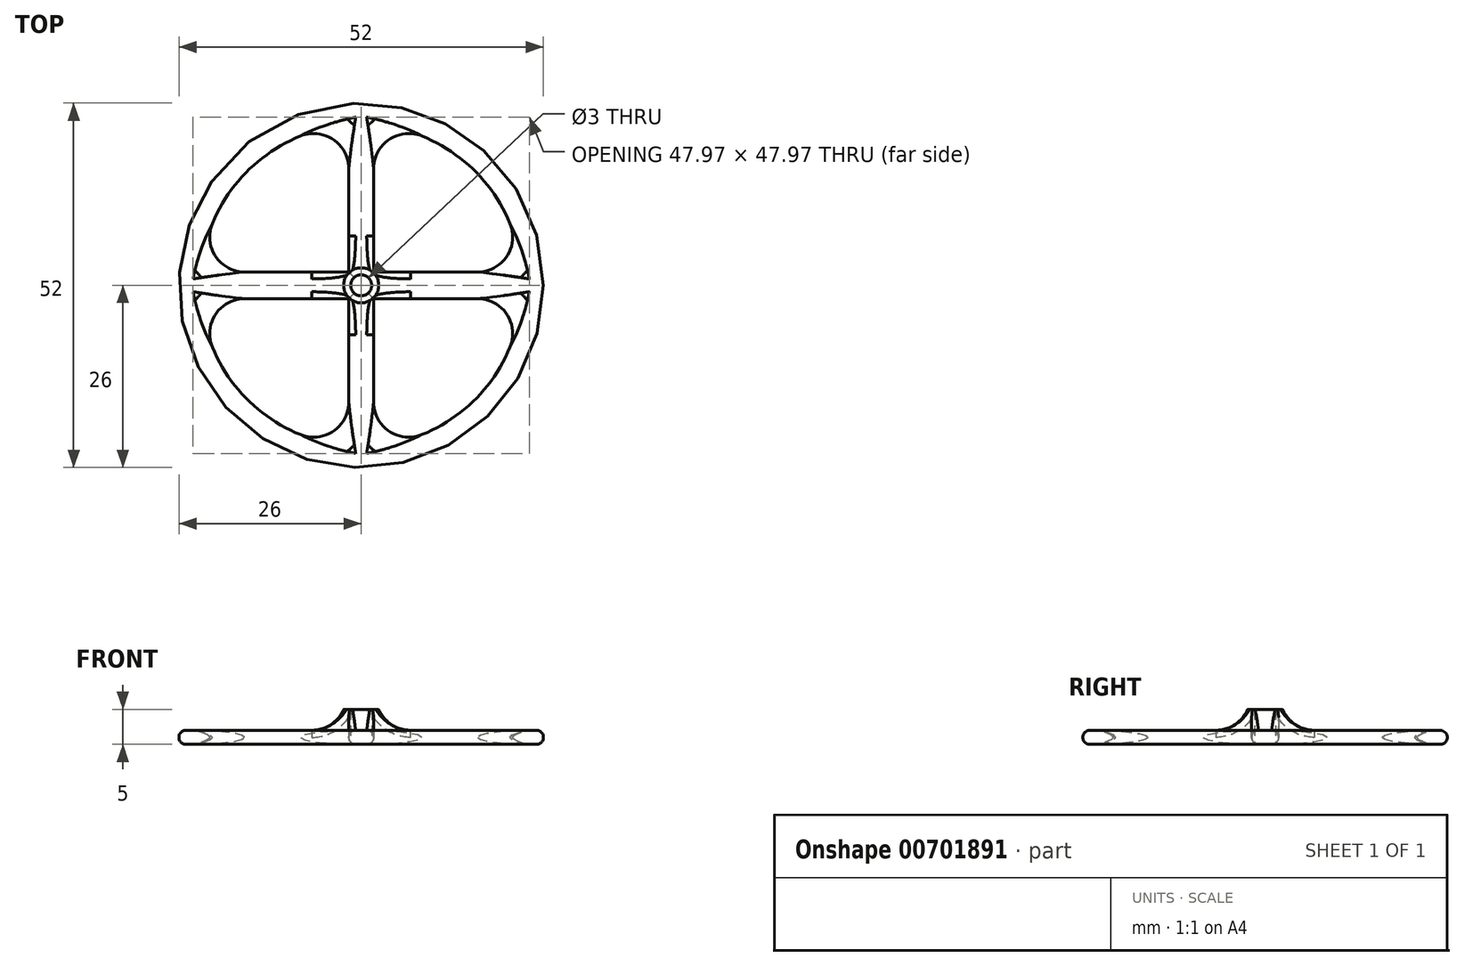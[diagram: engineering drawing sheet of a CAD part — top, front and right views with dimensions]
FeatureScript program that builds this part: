
annotation { "Feature Type Name" : "Feature", "Feature Type Description" : "" }
export const myFeature = defineFeature(function(context is Context, id is Id, definition is map)
    precondition{}
    {
        {
            var Q0;
            Q0=qCreatedBy(makeId("Top.planeOp"),FACE);
            var sketch = newSketch(context, id + "F0", { "sketchPlane" : qUnion([Q0])});
            skCircle(sketch, "E0", {"center": v(0, 0) * mm, "radius": 26 * mm});
            skLineSegment(sketch, "E1.bottom", {"start": v(1.78, -25.94) * mm, "end": v(-1.78, -25.94) * mm});
            skLineSegment(sketch, "E1.top", {"start": v(1.78, 25.94) * mm, "end": v(-1.78, 25.94) * mm});
            skLineSegment(sketch, "E1.left", {"start": v(1.78, -25.94) * mm, "end": v(1.78, 25.94) * mm});
            skLineSegment(sketch, "E1.right", {"start": v(-1.78, -25.94) * mm, "end": v(-1.78, 25.94) * mm});
            skLineSegment(sketch, "E2.bottom", {"start": v(25.93, -1.91) * mm, "end": v(-25.93, -1.91) * mm});
            skLineSegment(sketch, "E2.top", {"start": v(25.93, 1.91) * mm, "end": v(-25.93, 1.91) * mm});
            skLineSegment(sketch, "E2.left", {"start": v(25.93, -1.91) * mm, "end": v(25.93, 1.91) * mm});
            skLineSegment(sketch, "E2.right", {"start": v(-25.93, -1.91) * mm, "end": v(-25.93, 1.91) * mm});
            skCircle(sketch, "E3", {"center": v(0, 0) * mm, "radius": 1.57 * mm});
            skCircle(sketch, "E4", {"center": v(0, 0) * mm, "radius": 23 * mm});
            skSolve(sketch);
        }
        {
            var Q0;
            {var subQ0=sQuery(id+"F0.wireOp",EDGE,"E2.right");Q0=makeQuery(id+"F0.imprint","IMPRINT",FACE,{"disambiguationData":[TD([[makeQuery(id+"F0.imprint","IMPRINT",EDGE,{"derivedFrom":subQ0}),1.0]])]});}
            var Q1;
            {var subQ0=sQuery(id+"F0.wireOp",EDGE,"E2.right");Q1=makeQuery(id+"F0.imprint","IMPRINT",FACE,{"disambiguationData":[TD([[makeQuery(id+"F0.imprint","IMPRINT",EDGE,{"derivedFrom":subQ0}),-1.0]])]});}
            var Q2;
            {var subQ0=sQuery(id+"F0.wireOp",EDGE,"E1.right");var subQ5=sQuery(id+"F0.wireOp",EDGE,"E4");var subQ6=makeQuery(id+"F0.imprint","INTERSECT",VERTEX,{"disambiguationData":[OD(1.0)],"derivedFrom":[subQ0,subQ5]});Q2=makeQuery(id+"F0.imprint","IMPRINT",FACE,{"disambiguationData":[TD([[makeQuery(id+"F0.imprint","IMPRINT",EDGE,{"disambiguationData":[TD([[subQ6,-1.0]])],"derivedFrom":subQ5}),-1.0]])]});}
            var Q3;
            {var subQ0=sQuery(id+"F0.wireOp",EDGE,"E1.top");Q3=makeQuery(id+"F0.imprint","IMPRINT",FACE,{"disambiguationData":[TD([[makeQuery(id+"F0.imprint","IMPRINT",EDGE,{"derivedFrom":subQ0}),1.0]])]});}
            var Q4;
            {var subQ0=sQuery(id+"F0.wireOp",EDGE,"E1.top");Q4=makeQuery(id+"F0.imprint","IMPRINT",FACE,{"disambiguationData":[TD([[makeQuery(id+"F0.imprint","IMPRINT",EDGE,{"derivedFrom":subQ0}),-1.0]])]});}
            var Q5;
            {var subQ0=sQuery(id+"F0.wireOp",EDGE,"E2.left");Q5=makeQuery(id+"F0.imprint","IMPRINT",FACE,{"disambiguationData":[TD([[makeQuery(id+"F0.imprint","IMPRINT",EDGE,{"derivedFrom":subQ0}),-1.0]])]});}
            var Q6;
            {var subQ0=sQuery(id+"F0.wireOp",EDGE,"E2.left");Q6=makeQuery(id+"F0.imprint","IMPRINT",FACE,{"disambiguationData":[TD([[makeQuery(id+"F0.imprint","IMPRINT",EDGE,{"derivedFrom":subQ0}),1.0]])]});}
            var Q7;
            {var subQ0=sQuery(id+"F0.wireOp",EDGE,"E1.left");var subQ5=sQuery(id+"F0.wireOp",EDGE,"E4");var subQ7=makeQuery(id+"F0.imprint","INTERSECT",VERTEX,{"disambiguationData":[OD(1.0)],"derivedFrom":[subQ0,subQ5]});Q7=makeQuery(id+"F0.imprint","IMPRINT",FACE,{"disambiguationData":[TD([[makeQuery(id+"F0.imprint","IMPRINT",EDGE,{"disambiguationData":[TD([[subQ7,1.0]])],"derivedFrom":subQ5}),-1.0]])]});}
            var Q8;
            {var subQ0=sQuery(id+"F0.wireOp",EDGE,"E2.top");var subQ1=sQuery(id+"F0.wireOp",EDGE,"E1.left");var subQ2=makeQuery(id+"F0.imprint","INTERSECT",VERTEX,{"derivedFrom":[subQ1,subQ0]});Q8=makeQuery(id+"F0.imprint","IMPRINT",FACE,{"disambiguationData":[TD([[makeQuery(id+"F0.imprint","IMPRINT",EDGE,{"disambiguationData":[TD([[subQ2,-1.0]])],"derivedFrom":subQ1}),1.0]])]});}
            var Q9;
            Q9=makeQuery(id+"F0.imprint","IMPRINT",FACE,{"disambiguationData":[TD([[makeQuery(id+"F0.imprint","IMPRINT",EDGE,{"derivedFrom":sQuery(id+"F0.wireOp",EDGE,"E3")}),-1.0]])]});
            var Q10;
            {var subQ0=sQuery(id+"F0.wireOp",EDGE,"E2.bottom");var subQ1=sQuery(id+"F0.wireOp",EDGE,"E1.left");var subQ2=makeQuery(id+"F0.imprint","INTERSECT",VERTEX,{"derivedFrom":[subQ1,subQ0]});Q10=makeQuery(id+"F0.imprint","IMPRINT",FACE,{"disambiguationData":[TD([[makeQuery(id+"F0.imprint","IMPRINT",EDGE,{"disambiguationData":[TD([[subQ2,-1.0]])],"derivedFrom":subQ1}),-1.0]])]});}
            var Q11;
            {var subQ0=sQuery(id+"F0.wireOp",EDGE,"E2.bottom");var subQ1=sQuery(id+"F0.wireOp",EDGE,"E1.right");var subQ2=makeQuery(id+"F0.imprint","INTERSECT",VERTEX,{"derivedFrom":[subQ1,subQ0]});Q11=makeQuery(id+"F0.imprint","IMPRINT",FACE,{"disambiguationData":[TD([[makeQuery(id+"F0.imprint","IMPRINT",EDGE,{"disambiguationData":[TD([[subQ2,-1.0]])],"derivedFrom":subQ1}),1.0]])]});}
            var Q12;
            {var subQ0=sQuery(id+"F0.wireOp",EDGE,"E4");var subQ1=sQuery(id+"F0.wireOp",EDGE,"E1.left");var subQ2=makeQuery(id+"F0.imprint","INTERSECT",VERTEX,{"disambiguationData":[OD(0.0)],"derivedFrom":[subQ1,subQ0]});Q12=makeQuery(id+"F0.imprint","IMPRINT",FACE,{"disambiguationData":[TD([[makeQuery(id+"F0.imprint","IMPRINT",EDGE,{"disambiguationData":[TD([[subQ2,-1.0]])],"derivedFrom":subQ1}),1.0]])]});}
            var Q13;
            {var subQ0=sQuery(id+"F0.wireOp",EDGE,"E1.right");var subQ5=sQuery(id+"F0.wireOp",EDGE,"E4");var subQ7=makeQuery(id+"F0.imprint","INTERSECT",VERTEX,{"disambiguationData":[OD(0.0)],"derivedFrom":[subQ0,subQ5]});Q13=makeQuery(id+"F0.imprint","IMPRINT",FACE,{"disambiguationData":[TD([[makeQuery(id+"F0.imprint","IMPRINT",EDGE,{"disambiguationData":[TD([[subQ7,1.0]])],"derivedFrom":subQ5}),-1.0]])]});}
            var Q14;
            {var subQ0=sQuery(id+"F0.wireOp",EDGE,"E1.bottom");Q14=makeQuery(id+"F0.imprint","IMPRINT",FACE,{"disambiguationData":[TD([[makeQuery(id+"F0.imprint","IMPRINT",EDGE,{"derivedFrom":subQ0}),-1.0]])]});}
            var Q15;
            {var subQ0=sQuery(id+"F0.wireOp",EDGE,"E1.bottom");Q15=makeQuery(id+"F0.imprint","IMPRINT",FACE,{"disambiguationData":[TD([[makeQuery(id+"F0.imprint","IMPRINT",EDGE,{"derivedFrom":subQ0}),1.0]])]});}
            var Q16;
            {var subQ0=sQuery(id+"F0.wireOp",EDGE,"E1.left");var subQ5=sQuery(id+"F0.wireOp",EDGE,"E4");var subQ6=makeQuery(id+"F0.imprint","INTERSECT",VERTEX,{"disambiguationData":[OD(0.0)],"derivedFrom":[subQ0,subQ5]});Q16=makeQuery(id+"F0.imprint","IMPRINT",FACE,{"disambiguationData":[TD([[makeQuery(id+"F0.imprint","IMPRINT",EDGE,{"disambiguationData":[TD([[subQ6,-1.0]])],"derivedFrom":subQ5}),-1.0]])]});}
            extrude(context, id + "F1", {"entities" : qUnion([Q0, Q1, Q2, Q3, Q4, Q5, Q6, Q7, Q8, Q9, Q10, Q11, Q12, Q13, Q14, Q15, Q16]), "depth" : 2 * mm, "offsetDistance" : 25 * mm});
        }
        {
            var Q0;
            Q0=qCreatedBy(makeId("Top.planeOp"),FACE);
            var sketch = newSketch(context, id + "F2", { "sketchPlane" : qUnion([Q0])});
            skCircle(sketch, "E5", {"center": v(0, 0) * mm, "radius": 2.5 * mm});
            skSolve(sketch);
        }
        {
            var Q0;
            Q0=makeQuery(id+"F2.imprint","IMPRINT",FACE,{"disambiguationData":[TD([[makeQuery(id+"F2.imprint","IMPRINT",EDGE,{"derivedFrom":sQuery(id+"F2.wireOp",EDGE,"E5")}),1.0]])]});
            extrude(context, id + "F3", {"entities" : qUnion([Q0]), "operationType" : NewBodyOperationType.ADD, "depth" : 5 * mm, "offsetDistance" : 25 * mm});
        }
        {
            var Q0;
            Q0=qCreatedBy(makeId("Top.planeOp"),FACE);
            var sketch = newSketch(context, id + "F4", { "sketchPlane" : qUnion([Q0])});
            skCircle(sketch, "E6", {"center": v(0, 0) * mm, "radius": 1.5 * mm});
            skSolve(sketch);
        }
        {
            var Q0;
            Q0=makeQuery(id+"F4.imprint","IMPRINT",FACE,{"disambiguationData":[TD([[makeQuery(id+"F4.imprint","IMPRINT",EDGE,{"derivedFrom":sQuery(id+"F4.wireOp",EDGE,"E6")}),1.0]])]});
            extrude(context, id + "F5", {"entities" : qUnion([Q0]), "operationType" : NewBodyOperationType.REMOVE, "depth" : 5 * mm, "offsetDistance" : 25 * mm});
        }
        {
            var Q0;
            Q0=makeQuery(id+"F1.opExtrude","CAP_EDGE",EDGE,{"disambiguationData":[OSD([sQuery(id+"F0.wireOp",EDGE,"E0")])],"isStart":false});
            fillet(context, id + "F6", {"entities" : qUnion([Q0]), "tangentPropagation" : true, "radius" : 1 * mm, "defaultsChanged" : true, "vertexSettings" : [], "allowEdgeOverflow" : false});
        }
        {
            var Q0;
            Q0=makeQuery(id+"F1.opExtrude","CAP_EDGE",EDGE,{"disambiguationData":[OSD([sQuery(id+"F0.wireOp",EDGE,"E0")])],"isStart":true});
            fillet(context, id + "F7", {"entities" : qUnion([Q0]), "tangentPropagation" : true, "radius" : 1 * mm, "defaultsChanged" : true, "vertexSettings" : [], "allowEdgeOverflow" : false});
        }
        {
            var Q0;
            Q0=makeQuery(id+"F3.boolean.opBoolean","INTERSECT",EDGE,{"derivedFrom":[makeQuery(id+"F1.opExtrude","CAP_FACE",FACE,{"disambiguationData":[OSD([sQuery(id+"F0.wireOp",EDGE,"E0"),sQuery(id+"F0.wireOp",EDGE,"E1.left"),sQuery(id+"F0.wireOp",EDGE,"E1.right"),sQuery(id+"F0.wireOp",EDGE,"E2.bottom"),sQuery(id+"F0.wireOp",EDGE,"E2.top"),sQuery(id+"F0.wireOp",EDGE,"E3"),sQuery(id+"F0.wireOp",EDGE,"E4")])],"isStart":false}),makeQuery(id+"F3.opExtrude","SWEPT_FACE",FACE,{"disambiguationData":[OSD([sQuery(id+"F2.wireOp",EDGE,"E5")])]})]});
            fillet(context, id + "F8", {"entities" : qUnion([Q0]), "tangentPropagation" : true, "radius" : 5 * mm, "defaultsChanged" : false, "vertexSettings" : [], "allowEdgeOverflow" : false});
        }
        {
            var Q0;
            {var subQ0=sQuery(id+"F0.wireOp",EDGE,"E1.right");Q0=makeQuery(id+"F1.opExtrude","CAP_EDGE",EDGE,{"disambiguationData":[OSD([subQ0]),TDD([makeQuery(id+"F0.imprint","IMPRINT",EDGE,{"disambiguationData":[TD([[makeQuery(id+"F0.imprint","INTERSECT",VERTEX,{"disambiguationData":[OD(0.0)],"derivedFrom":[subQ0,sQuery(id+"F0.wireOp",EDGE,"E4")]}),-1.0]])],"derivedFrom":subQ0})])],"isStart":true});}
            var Q1;
            {var subQ0=sQuery(id+"F0.wireOp",EDGE,"E1.left");Q1=makeQuery(id+"F1.opExtrude","CAP_EDGE",EDGE,{"disambiguationData":[OSD([subQ0]),TDD([makeQuery(id+"F0.imprint","IMPRINT",EDGE,{"disambiguationData":[TD([[makeQuery(id+"F0.imprint","INTERSECT",VERTEX,{"disambiguationData":[OD(0.0)],"derivedFrom":[subQ0,sQuery(id+"F0.wireOp",EDGE,"E4")]}),-1.0]])],"derivedFrom":subQ0})])],"isStart":true});}
            var Q2;
            {var subQ0=sQuery(id+"F0.wireOp",EDGE,"E1.left");Q2=makeQuery(id+"F1.opExtrude","CAP_EDGE",EDGE,{"disambiguationData":[OSD([subQ0]),TDD([makeQuery(id+"F0.imprint","IMPRINT",EDGE,{"disambiguationData":[TD([[makeQuery(id+"F0.imprint","INTERSECT",VERTEX,{"derivedFrom":[subQ0,sQuery(id+"F0.wireOp",EDGE,"E2.top")]}),-1.0]])],"derivedFrom":subQ0})])],"isStart":true});}
            var Q3;
            {var subQ0=sQuery(id+"F0.wireOp",EDGE,"E1.right");Q3=makeQuery(id+"F1.opExtrude","CAP_EDGE",EDGE,{"disambiguationData":[OSD([subQ0]),TDD([makeQuery(id+"F0.imprint","IMPRINT",EDGE,{"disambiguationData":[TD([[makeQuery(id+"F0.imprint","INTERSECT",VERTEX,{"derivedFrom":[subQ0,sQuery(id+"F0.wireOp",EDGE,"E2.top")]}),-1.0]])],"derivedFrom":subQ0})])],"isStart":true});}
            var Q4;
            {var subQ0=sQuery(id+"F0.wireOp",EDGE,"E2.bottom");Q4=makeQuery(id+"F1.opExtrude","CAP_EDGE",EDGE,{"disambiguationData":[OSD([subQ0]),TDD([makeQuery(id+"F0.imprint","IMPRINT",EDGE,{"disambiguationData":[TD([[makeQuery(id+"F0.imprint","INTERSECT",VERTEX,{"derivedFrom":[sQuery(id+"F0.wireOp",EDGE,"E1.right"),subQ0]}),-1.0]])],"derivedFrom":subQ0})])],"isStart":true});}
            var Q5;
            {var subQ0=sQuery(id+"F0.wireOp",EDGE,"E2.top");Q5=makeQuery(id+"F1.opExtrude","CAP_EDGE",EDGE,{"disambiguationData":[OSD([subQ0]),TDD([makeQuery(id+"F0.imprint","IMPRINT",EDGE,{"disambiguationData":[TD([[makeQuery(id+"F0.imprint","INTERSECT",VERTEX,{"derivedFrom":[sQuery(id+"F0.wireOp",EDGE,"E1.right"),subQ0]}),-1.0]])],"derivedFrom":subQ0})])],"isStart":true});}
            var Q6;
            {var subQ0=sQuery(id+"F0.wireOp",EDGE,"E2.top");Q6=makeQuery(id+"F1.opExtrude","CAP_EDGE",EDGE,{"disambiguationData":[OSD([subQ0]),TDD([makeQuery(id+"F0.imprint","IMPRINT",EDGE,{"disambiguationData":[TD([[makeQuery(id+"F0.imprint","INTERSECT",VERTEX,{"derivedFrom":[sQuery(id+"F0.wireOp",EDGE,"E1.left"),subQ0]}),1.0]])],"derivedFrom":subQ0})])],"isStart":true});}
            var Q7;
            {var subQ0=sQuery(id+"F0.wireOp",EDGE,"E2.bottom");Q7=makeQuery(id+"F1.opExtrude","CAP_EDGE",EDGE,{"disambiguationData":[OSD([subQ0]),TDD([makeQuery(id+"F0.imprint","IMPRINT",EDGE,{"disambiguationData":[TD([[makeQuery(id+"F0.imprint","INTERSECT",VERTEX,{"derivedFrom":[sQuery(id+"F0.wireOp",EDGE,"E1.left"),subQ0]}),1.0]])],"derivedFrom":subQ0})])],"isStart":true});}
            var Q8;
            {var subQ0=sQuery(id+"F0.wireOp",EDGE,"E4");Q8=makeQuery(id+"F1.opExtrude","CAP_EDGE",EDGE,{"disambiguationData":[OSD([subQ0]),TDD([makeQuery(id+"F0.imprint","IMPRINT",EDGE,{"disambiguationData":[TD([[makeQuery(id+"F0.imprint","INTERSECT",VERTEX,{"disambiguationData":[OD(1.0)],"derivedFrom":[sQuery(id+"F0.wireOp",EDGE,"E1.right"),subQ0]}),-1.0]])],"derivedFrom":subQ0})])],"isStart":true});}
            var Q9;
            {var subQ0=sQuery(id+"F0.wireOp",EDGE,"E4");Q9=makeQuery(id+"F1.opExtrude","CAP_EDGE",EDGE,{"disambiguationData":[OSD([subQ0]),TDD([makeQuery(id+"F0.imprint","IMPRINT",EDGE,{"disambiguationData":[TD([[makeQuery(id+"F0.imprint","INTERSECT",VERTEX,{"disambiguationData":[OD(1.0)],"derivedFrom":[sQuery(id+"F0.wireOp",EDGE,"E1.left"),subQ0]}),1.0]])],"derivedFrom":subQ0})])],"isStart":true});}
            var Q10;
            {var subQ0=sQuery(id+"F0.wireOp",EDGE,"E4");Q10=makeQuery(id+"F1.opExtrude","CAP_EDGE",EDGE,{"disambiguationData":[OSD([subQ0]),TDD([makeQuery(id+"F0.imprint","IMPRINT",EDGE,{"disambiguationData":[TD([[makeQuery(id+"F0.imprint","INTERSECT",VERTEX,{"disambiguationData":[OD(0.0)],"derivedFrom":[sQuery(id+"F0.wireOp",EDGE,"E1.right"),subQ0]}),1.0]])],"derivedFrom":subQ0})])],"isStart":true});}
            var Q11;
            {var subQ0=sQuery(id+"F0.wireOp",EDGE,"E4");Q11=makeQuery(id+"F1.opExtrude","CAP_EDGE",EDGE,{"disambiguationData":[OSD([subQ0]),TDD([makeQuery(id+"F0.imprint","IMPRINT",EDGE,{"disambiguationData":[TD([[makeQuery(id+"F0.imprint","INTERSECT",VERTEX,{"disambiguationData":[OD(0.0)],"derivedFrom":[sQuery(id+"F0.wireOp",EDGE,"E1.left"),subQ0]}),-1.0]])],"derivedFrom":subQ0})])],"isStart":true});}
            var Q12;
            {var subQ0=sQuery(id+"F0.wireOp",EDGE,"E4");Q12=makeQuery(id+"F1.opExtrude","CAP_EDGE",EDGE,{"disambiguationData":[OSD([subQ0]),TDD([makeQuery(id+"F0.imprint","IMPRINT",EDGE,{"disambiguationData":[TD([[makeQuery(id+"F0.imprint","INTERSECT",VERTEX,{"disambiguationData":[OD(1.0)],"derivedFrom":[sQuery(id+"F0.wireOp",EDGE,"E1.right"),subQ0]}),-1.0]])],"derivedFrom":subQ0})])],"isStart":false});}
            var Q13;
            {var subQ0=sQuery(id+"F0.wireOp",EDGE,"E4");Q13=makeQuery(id+"F1.opExtrude","CAP_EDGE",EDGE,{"disambiguationData":[OSD([subQ0]),TDD([makeQuery(id+"F0.imprint","IMPRINT",EDGE,{"disambiguationData":[TD([[makeQuery(id+"F0.imprint","INTERSECT",VERTEX,{"disambiguationData":[OD(1.0)],"derivedFrom":[sQuery(id+"F0.wireOp",EDGE,"E1.left"),subQ0]}),1.0]])],"derivedFrom":subQ0})])],"isStart":false});}
            var Q14;
            {var subQ0=sQuery(id+"F0.wireOp",EDGE,"E4");Q14=makeQuery(id+"F1.opExtrude","CAP_EDGE",EDGE,{"disambiguationData":[OSD([subQ0]),TDD([makeQuery(id+"F0.imprint","IMPRINT",EDGE,{"disambiguationData":[TD([[makeQuery(id+"F0.imprint","INTERSECT",VERTEX,{"disambiguationData":[OD(0.0)],"derivedFrom":[sQuery(id+"F0.wireOp",EDGE,"E1.left"),subQ0]}),-1.0]])],"derivedFrom":subQ0})])],"isStart":false});}
            var Q15;
            {var subQ0=sQuery(id+"F0.wireOp",EDGE,"E4");Q15=makeQuery(id+"F1.opExtrude","CAP_EDGE",EDGE,{"disambiguationData":[OSD([subQ0]),TDD([makeQuery(id+"F0.imprint","IMPRINT",EDGE,{"disambiguationData":[TD([[makeQuery(id+"F0.imprint","INTERSECT",VERTEX,{"disambiguationData":[OD(0.0)],"derivedFrom":[sQuery(id+"F0.wireOp",EDGE,"E1.right"),subQ0]}),1.0]])],"derivedFrom":subQ0})])],"isStart":false});}
            var Q16;
            {var subQ0=sQuery(id+"F0.wireOp",EDGE,"E2.bottom");Q16=makeQuery(id+"F1.opExtrude","CAP_EDGE",EDGE,{"disambiguationData":[OSD([subQ0]),TDD([makeQuery(id+"F0.imprint","IMPRINT",EDGE,{"disambiguationData":[TD([[makeQuery(id+"F0.imprint","INTERSECT",VERTEX,{"derivedFrom":[sQuery(id+"F0.wireOp",EDGE,"E1.left"),subQ0]}),1.0]])],"derivedFrom":subQ0})])],"isStart":false});}
            var Q17;
            {var subQ0=sQuery(id+"F0.wireOp",EDGE,"E2.top");Q17=makeQuery(id+"F1.opExtrude","CAP_EDGE",EDGE,{"disambiguationData":[OSD([subQ0]),TDD([makeQuery(id+"F0.imprint","IMPRINT",EDGE,{"disambiguationData":[TD([[makeQuery(id+"F0.imprint","INTERSECT",VERTEX,{"derivedFrom":[sQuery(id+"F0.wireOp",EDGE,"E1.left"),subQ0]}),1.0]])],"derivedFrom":subQ0})])],"isStart":false});}
            var Q18;
            {var subQ0=sQuery(id+"F0.wireOp",EDGE,"E1.left");Q18=makeQuery(id+"F1.opExtrude","CAP_EDGE",EDGE,{"disambiguationData":[OSD([subQ0]),TDD([makeQuery(id+"F0.imprint","IMPRINT",EDGE,{"disambiguationData":[TD([[makeQuery(id+"F0.imprint","INTERSECT",VERTEX,{"derivedFrom":[subQ0,sQuery(id+"F0.wireOp",EDGE,"E2.top")]}),-1.0]])],"derivedFrom":subQ0})])],"isStart":false});}
            var Q19;
            {var subQ0=sQuery(id+"F0.wireOp",EDGE,"E1.right");Q19=makeQuery(id+"F1.opExtrude","CAP_EDGE",EDGE,{"disambiguationData":[OSD([subQ0]),TDD([makeQuery(id+"F0.imprint","IMPRINT",EDGE,{"disambiguationData":[TD([[makeQuery(id+"F0.imprint","INTERSECT",VERTEX,{"derivedFrom":[subQ0,sQuery(id+"F0.wireOp",EDGE,"E2.top")]}),-1.0]])],"derivedFrom":subQ0})])],"isStart":false});}
            var Q20;
            {var subQ0=sQuery(id+"F0.wireOp",EDGE,"E2.bottom");Q20=makeQuery(id+"F1.opExtrude","CAP_EDGE",EDGE,{"disambiguationData":[OSD([subQ0]),TDD([makeQuery(id+"F0.imprint","IMPRINT",EDGE,{"disambiguationData":[TD([[makeQuery(id+"F0.imprint","INTERSECT",VERTEX,{"derivedFrom":[sQuery(id+"F0.wireOp",EDGE,"E1.right"),subQ0]}),-1.0]])],"derivedFrom":subQ0})])],"isStart":false});}
            var Q21;
            {var subQ0=sQuery(id+"F0.wireOp",EDGE,"E2.top");Q21=makeQuery(id+"F1.opExtrude","CAP_EDGE",EDGE,{"disambiguationData":[OSD([subQ0]),TDD([makeQuery(id+"F0.imprint","IMPRINT",EDGE,{"disambiguationData":[TD([[makeQuery(id+"F0.imprint","INTERSECT",VERTEX,{"derivedFrom":[sQuery(id+"F0.wireOp",EDGE,"E1.right"),subQ0]}),-1.0]])],"derivedFrom":subQ0})])],"isStart":false});}
            var Q22;
            {var subQ0=sQuery(id+"F0.wireOp",EDGE,"E1.right");Q22=makeQuery(id+"F1.opExtrude","CAP_EDGE",EDGE,{"disambiguationData":[OSD([subQ0]),TDD([makeQuery(id+"F0.imprint","IMPRINT",EDGE,{"disambiguationData":[TD([[makeQuery(id+"F0.imprint","INTERSECT",VERTEX,{"disambiguationData":[OD(0.0)],"derivedFrom":[subQ0,sQuery(id+"F0.wireOp",EDGE,"E4")]}),-1.0]])],"derivedFrom":subQ0})])],"isStart":false});}
            var Q23;
            {var subQ0=sQuery(id+"F0.wireOp",EDGE,"E1.left");Q23=makeQuery(id+"F1.opExtrude","CAP_EDGE",EDGE,{"disambiguationData":[OSD([subQ0]),TDD([makeQuery(id+"F0.imprint","IMPRINT",EDGE,{"disambiguationData":[TD([[makeQuery(id+"F0.imprint","INTERSECT",VERTEX,{"disambiguationData":[OD(0.0)],"derivedFrom":[subQ0,sQuery(id+"F0.wireOp",EDGE,"E4")]}),-1.0]])],"derivedFrom":subQ0})])],"isStart":false});}
            fillet(context, id + "F9", {"entities" : qUnion([Q0, Q1, Q2, Q3, Q4, Q5, Q6, Q7, Q8, Q9, Q10, Q11, Q12, Q13, Q14, Q15, Q16, Q17, Q18, Q19, Q20, Q21, Q22, Q23]), "tangentPropagation" : true, "radius" : 1 * mm, "defaultsChanged" : false, "vertexSettings" : [], "allowEdgeOverflow" : false});
        }
        {
            var Q0;
            {var subQ0=sQuery(id+"F0.wireOp",EDGE,"E4");var subQ1=sQuery(id+"F0.wireOp",EDGE,"E1.left");var subQ2=makeQuery(id+"F0.imprint","INTERSECT",VERTEX,{"disambiguationData":[OD(0.0)],"derivedFrom":[subQ1,subQ0]});Q0=makeQuery(id+"F9.opFillet","BLEND_EDGE",EDGE,{"blendedFrom":[makeQuery(id+"F1.opExtrude","CAP_EDGE",EDGE,{"disambiguationData":[OSD([subQ0]),TDD([makeQuery(id+"F0.imprint","IMPRINT",EDGE,{"disambiguationData":[TD([[subQ2,-1.0]])],"derivedFrom":subQ0})])],"isStart":false}),makeQuery(id+"F1.opExtrude","CAP_EDGE",EDGE,{"disambiguationData":[OSD([subQ1]),TDD([makeQuery(id+"F0.imprint","IMPRINT",EDGE,{"disambiguationData":[TD([[subQ2,-1.0]])],"derivedFrom":subQ1})])],"isStart":false})],"blendedInto":[]});}
            var Q1;
            {var subQ0=sQuery(id+"F0.wireOp",EDGE,"E4");var subQ1=sQuery(id+"F0.wireOp",EDGE,"E1.right");var subQ2=makeQuery(id+"F0.imprint","INTERSECT",VERTEX,{"disambiguationData":[OD(0.0)],"derivedFrom":[subQ1,subQ0]});Q1=makeQuery(id+"F9.opFillet","BLEND_EDGE",EDGE,{"blendedFrom":[makeQuery(id+"F1.opExtrude","CAP_EDGE",EDGE,{"disambiguationData":[OSD([subQ0]),TDD([makeQuery(id+"F0.imprint","IMPRINT",EDGE,{"disambiguationData":[TD([[subQ2,1.0]])],"derivedFrom":subQ0})])],"isStart":false}),makeQuery(id+"F1.opExtrude","CAP_EDGE",EDGE,{"disambiguationData":[OSD([subQ1]),TDD([makeQuery(id+"F0.imprint","IMPRINT",EDGE,{"disambiguationData":[TD([[subQ2,-1.0]])],"derivedFrom":subQ1})])],"isStart":false})],"blendedInto":[]});}
            var Q2;
            {var subQ0=sQuery(id+"F0.wireOp",EDGE,"E2.top");var subQ1=sQuery(id+"F0.wireOp",EDGE,"E1.left");var subQ2=sQuery(id+"F0.wireOp",EDGE,"E4");Q2=makeQuery(id+"F9.opFillet","BLEND_EDGE",EDGE,{"blendedFrom":[makeQuery(id+"F1.opExtrude","CAP_EDGE",EDGE,{"disambiguationData":[OSD([subQ2]),TDD([makeQuery(id+"F0.imprint","IMPRINT",EDGE,{"disambiguationData":[TD([[makeQuery(id+"F0.imprint","INTERSECT",VERTEX,{"disambiguationData":[OD(1.0)],"derivedFrom":[subQ1,subQ2]}),1.0]])],"derivedFrom":subQ2})])],"isStart":false}),makeQuery(id+"F1.opExtrude","CAP_EDGE",EDGE,{"disambiguationData":[OSD([subQ0]),TDD([makeQuery(id+"F0.imprint","IMPRINT",EDGE,{"disambiguationData":[TD([[makeQuery(id+"F0.imprint","INTERSECT",VERTEX,{"derivedFrom":[subQ1,subQ0]}),1.0]])],"derivedFrom":subQ0})])],"isStart":false})],"blendedInto":[]});}
            var Q3;
            {var subQ0=sQuery(id+"F0.wireOp",EDGE,"E2.bottom");var subQ1=sQuery(id+"F0.wireOp",EDGE,"E1.left");var subQ2=sQuery(id+"F0.wireOp",EDGE,"E4");Q3=makeQuery(id+"F9.opFillet","BLEND_EDGE",EDGE,{"blendedFrom":[makeQuery(id+"F1.opExtrude","CAP_EDGE",EDGE,{"disambiguationData":[OSD([subQ2]),TDD([makeQuery(id+"F0.imprint","IMPRINT",EDGE,{"disambiguationData":[TD([[makeQuery(id+"F0.imprint","INTERSECT",VERTEX,{"disambiguationData":[OD(0.0)],"derivedFrom":[subQ1,subQ2]}),-1.0]])],"derivedFrom":subQ2})])],"isStart":false}),makeQuery(id+"F1.opExtrude","CAP_EDGE",EDGE,{"disambiguationData":[OSD([subQ0]),TDD([makeQuery(id+"F0.imprint","IMPRINT",EDGE,{"disambiguationData":[TD([[makeQuery(id+"F0.imprint","INTERSECT",VERTEX,{"derivedFrom":[subQ1,subQ0]}),1.0]])],"derivedFrom":subQ0})])],"isStart":false})],"blendedInto":[]});}
            var Q4;
            {var subQ0=sQuery(id+"F0.wireOp",EDGE,"E2.top");var subQ1=sQuery(id+"F0.wireOp",EDGE,"E1.left");var subQ2=sQuery(id+"F0.wireOp",EDGE,"E4");var subQ3=makeQuery(id+"F0.imprint","INTERSECT",VERTEX,{"disambiguationData":[OD(1.0)],"derivedFrom":[subQ1,subQ2]});Q4=makeQuery(id+"F9.opFillet","BLEND_EDGE",EDGE,{"blendedFrom":[makeQuery(id+"F1.opExtrude","CAP_EDGE",EDGE,{"disambiguationData":[OSD([subQ2]),TDD([makeQuery(id+"F0.imprint","IMPRINT",EDGE,{"disambiguationData":[TD([[subQ3,1.0]])],"derivedFrom":subQ2})])],"isStart":false}),makeQuery(id+"F1.opExtrude","CAP_EDGE",EDGE,{"disambiguationData":[OSD([subQ1]),TDD([makeQuery(id+"F0.imprint","IMPRINT",EDGE,{"disambiguationData":[TD([[makeQuery(id+"F0.imprint","INTERSECT",VERTEX,{"derivedFrom":[subQ1,subQ0]}),-1.0]])],"derivedFrom":subQ1})])],"isStart":false})],"blendedInto":[]});}
            var Q5;
            {var subQ0=sQuery(id+"F0.wireOp",EDGE,"E2.top");var subQ1=sQuery(id+"F0.wireOp",EDGE,"E1.right");var subQ2=sQuery(id+"F0.wireOp",EDGE,"E4");var subQ3=makeQuery(id+"F0.imprint","INTERSECT",VERTEX,{"disambiguationData":[OD(1.0)],"derivedFrom":[subQ1,subQ2]});Q5=makeQuery(id+"F9.opFillet","BLEND_EDGE",EDGE,{"blendedFrom":[makeQuery(id+"F1.opExtrude","CAP_EDGE",EDGE,{"disambiguationData":[OSD([subQ2]),TDD([makeQuery(id+"F0.imprint","IMPRINT",EDGE,{"disambiguationData":[TD([[subQ3,-1.0]])],"derivedFrom":subQ2})])],"isStart":false}),makeQuery(id+"F1.opExtrude","CAP_EDGE",EDGE,{"disambiguationData":[OSD([subQ1]),TDD([makeQuery(id+"F0.imprint","IMPRINT",EDGE,{"disambiguationData":[TD([[makeQuery(id+"F0.imprint","INTERSECT",VERTEX,{"derivedFrom":[subQ1,subQ0]}),-1.0]])],"derivedFrom":subQ1})])],"isStart":false})],"blendedInto":[]});}
            var Q6;
            {var subQ0=sQuery(id+"F0.wireOp",EDGE,"E2.top");var subQ1=sQuery(id+"F0.wireOp",EDGE,"E1.right");var subQ2=sQuery(id+"F0.wireOp",EDGE,"E4");Q6=makeQuery(id+"F9.opFillet","BLEND_EDGE",EDGE,{"blendedFrom":[makeQuery(id+"F1.opExtrude","CAP_EDGE",EDGE,{"disambiguationData":[OSD([subQ2]),TDD([makeQuery(id+"F0.imprint","IMPRINT",EDGE,{"disambiguationData":[TD([[makeQuery(id+"F0.imprint","INTERSECT",VERTEX,{"disambiguationData":[OD(1.0)],"derivedFrom":[subQ1,subQ2]}),-1.0]])],"derivedFrom":subQ2})])],"isStart":false}),makeQuery(id+"F1.opExtrude","CAP_EDGE",EDGE,{"disambiguationData":[OSD([subQ0]),TDD([makeQuery(id+"F0.imprint","IMPRINT",EDGE,{"disambiguationData":[TD([[makeQuery(id+"F0.imprint","INTERSECT",VERTEX,{"derivedFrom":[subQ1,subQ0]}),-1.0]])],"derivedFrom":subQ0})])],"isStart":false})],"blendedInto":[]});}
            var Q7;
            {var subQ0=sQuery(id+"F0.wireOp",EDGE,"E2.bottom");var subQ1=sQuery(id+"F0.wireOp",EDGE,"E1.right");var subQ2=sQuery(id+"F0.wireOp",EDGE,"E4");Q7=makeQuery(id+"F9.opFillet","BLEND_EDGE",EDGE,{"blendedFrom":[makeQuery(id+"F1.opExtrude","CAP_EDGE",EDGE,{"disambiguationData":[OSD([subQ2]),TDD([makeQuery(id+"F0.imprint","IMPRINT",EDGE,{"disambiguationData":[TD([[makeQuery(id+"F0.imprint","INTERSECT",VERTEX,{"disambiguationData":[OD(0.0)],"derivedFrom":[subQ1,subQ2]}),1.0]])],"derivedFrom":subQ2})])],"isStart":false}),makeQuery(id+"F1.opExtrude","CAP_EDGE",EDGE,{"disambiguationData":[OSD([subQ0]),TDD([makeQuery(id+"F0.imprint","IMPRINT",EDGE,{"disambiguationData":[TD([[makeQuery(id+"F0.imprint","INTERSECT",VERTEX,{"derivedFrom":[subQ1,subQ0]}),-1.0]])],"derivedFrom":subQ0})])],"isStart":false})],"blendedInto":[]});}
            fillet(context, id + "F10", {"entities" : qUnion([Q0, Q1, Q2, Q3, Q4, Q5, Q6, Q7]), "tangentPropagation" : true, "radius" : 5 * mm, "defaultsChanged" : false, "vertexSettings" : [], "allowEdgeOverflow" : false});
        }
    });
